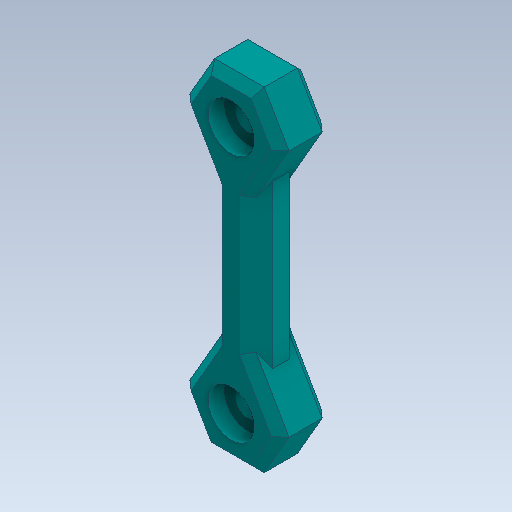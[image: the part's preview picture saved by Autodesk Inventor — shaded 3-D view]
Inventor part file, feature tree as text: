
AUTODESK INVENTOR PART (.ipt)
format: ipt  version: 2020 (Build 240168000, 168)  size: 164,352 bytes
history: native  units: in
note: dims shown in document units (in); Inventor stores cm internally (conversion verified against a paired STEP export)
features: other x3, sketch x2
ambient origin geometry x8: Origin, YZ Plane, XZ Plane, XY Plane, X Axis, Y Axis, Z Axis, Center Point
bodies: Solid1 (feature_tree)
feature tree (5):
  other  "Tibia Joint.ipt"
  other  "Solid1::Tibia Joint.ipt"
  other  "TaggingFeature1"
  sketch  "Sketch1"  dims[d0=0.3937in]
  sketch  "Sketch2"
